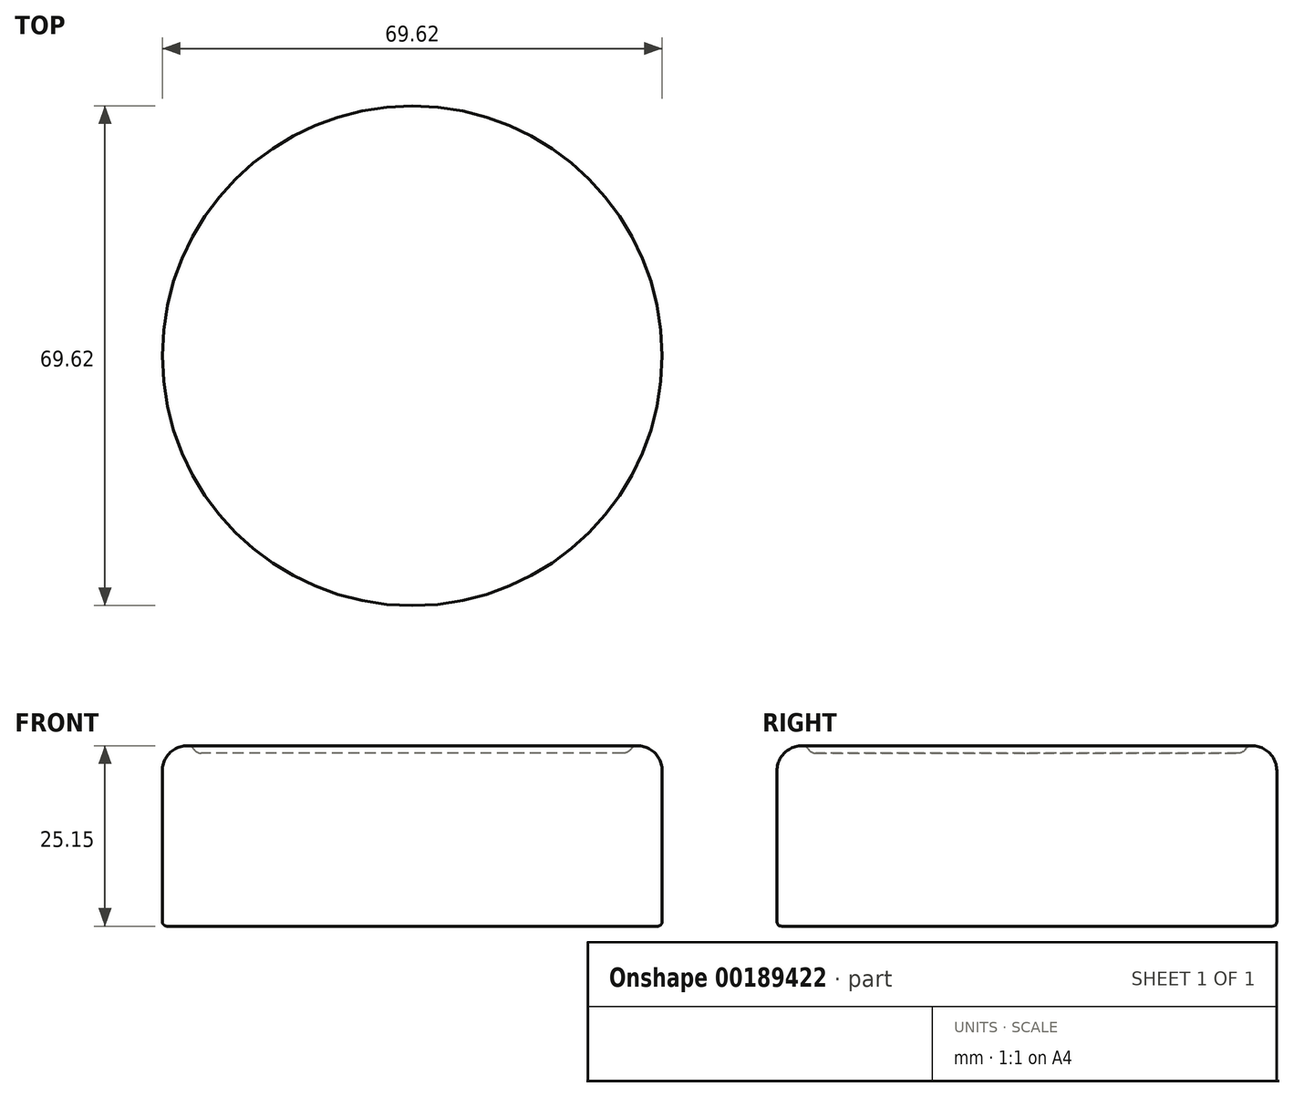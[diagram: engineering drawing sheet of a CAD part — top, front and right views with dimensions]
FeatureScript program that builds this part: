
annotation { "Feature Type Name" : "Feature", "Feature Type Description" : "" }
export const myFeature = defineFeature(function(context is Context, id is Id, definition is map)
    precondition{}
    {
        {
            var Q0;
            Q0=qCreatedBy(makeId("Top.planeOp"),FACE);
            var sketch = newSketch(context, id + "F0", { "sketchPlane" : qUnion([Q0])});
            skCircle(sketch, "E0", {"center": v(0, 0) * mm, "radius": 34.81 * mm});
            skSolve(sketch);
        }
        {
            var Q0;
            Q0 = qSketchRegion(id + "F0", true);
            extrude(context, id + "F1", {"entities" : qUnion([Q0]), "depth" : 25.15 * mm});
        }
        {
            var Q0;
            Q0=makeQuery(id+"F1.opExtrude","CAP_EDGE",EDGE,{"disambiguationData":[OSD([sQuery(id+"F0.wireOp",EDGE,"E0")])],"isStart":false});
            fillet(context, id + "F2", {"entities" : qUnion([Q0]), "radius" : 3.48 * mm, "tangentPropagation" : true, "allowEdgeOverflow" : false});
        }
        {
            var Q0;
            Q0=makeQuery(id+"F1.opExtrude","CAP_EDGE",EDGE,{"disambiguationData":[OSD([sQuery(id+"F0.wireOp",EDGE,"E0")])],"isStart":true});
            fillet(context, id + "F3", {"entities" : qUnion([Q0]), "radius" : 0.64 * mm, "tangentPropagation" : true, "allowEdgeOverflow" : false});
        }
        {
            var Q0;
            Q0=qCreatedBy(makeId("Front.planeOp"),FACE);
            var sketch = newSketch(context, id + "F4", { "sketchPlane" : qUnion([Q0])});
            skLineSegment(sketch, "E1", {"start": v(0, 24.1) * mm, "end": v(0, 25.15) * mm});
            skLineSegment(sketch, "E2", {"start": v(0, 25.15) * mm, "end": v(31.33, 25.15) * mm});
            skArc(sketch, "E3", {"start": v(31.33, 25.15) * mm, "mid": v(30.6, 24.84) * mm, "end": v(30.29, 24.1) * mm});
            skLineSegment(sketch, "E4", {"start": v(0, 24.1) * mm, "end": v(30.29, 24.1) * mm});
            skSolve(sketch);
        }
        {
            var Q0;
            Q0 = qSketchRegion(id + "F4", true);
            var Q1;
            Q1=sQuery(id+"F4.wireOp",EDGE,"E1");
            revolve(context, id + "F5", {"operationType" : NewBodyOperationType.REMOVE, "entities" : qUnion([Q0]), "axis" : qUnion([Q1]), "revolveType" : RevolveType.FULL, "oppositeDirection" : true});
        }
        {
            var Q0;
            Q0=makeQuery(id+"F5.boolean.opBoolean","COPY",EDGE,{"derivedFrom":makeQuery(id+"F5.opRevolve","SWEPT_EDGE",EDGE,{"disambiguationData":[OSD([sQuery(id+"F4.wireOp",EDGE,"E3"),sQuery(id+"F4.wireOp",EDGE,"E4")])]})});
            fillet(context, id + "F6", {"entities" : qUnion([Q0]), "radius" : 1.27 * mm, "tangentPropagation" : true, "allowEdgeOverflow" : false});
        }
    });
